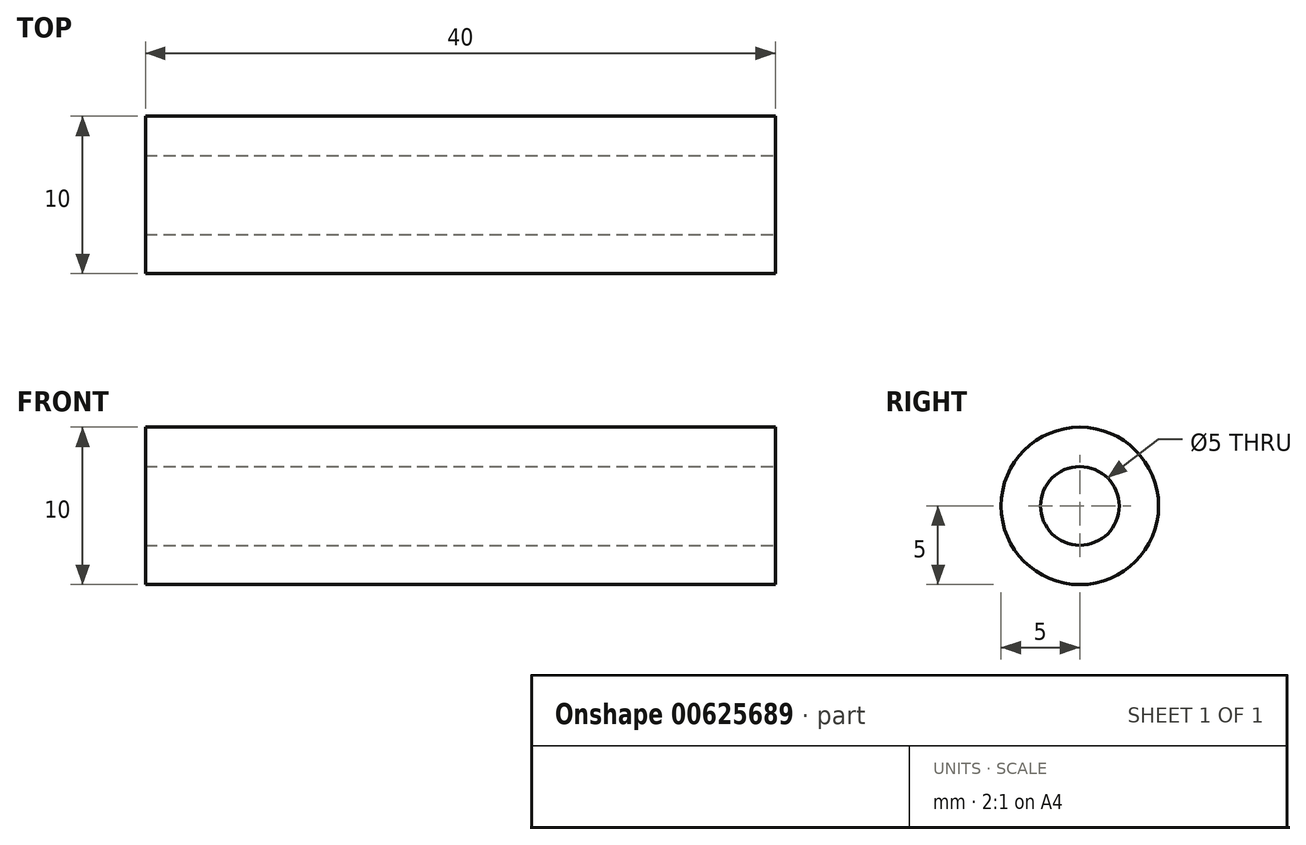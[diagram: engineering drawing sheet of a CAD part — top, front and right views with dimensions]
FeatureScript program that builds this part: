
annotation { "Feature Type Name" : "Feature", "Feature Type Description" : "" }
export const myFeature = defineFeature(function(context is Context, id is Id, definition is map)
    precondition{}
    {
        {
            var Q0;
            Q0=qCreatedBy(makeId("Right.planeOp"),FACE);
            var sketch = newSketch(context, id + "F0", { "sketchPlane" : qUnion([Q0])});
            skCircle(sketch, "E0", {"center": v(0, 0) * mm, "radius": 5 * mm});
            skSolve(sketch);
        }
        {
            var Q0;
            Q0 = qSketchRegion(id + "F0", true);
            extrude(context, id + "F1", {"entities" : qUnion([Q0]), "oppositeDirection" : true, "depth" : 40 * mm, "offsetDistance" : 25 * mm});
        }
        {
            var Q0;
            Q0=makeQuery(id+"F1.opExtrude","CAP_FACE",FACE,{"disambiguationData":[OSD([sQuery(id+"F0.wireOp",EDGE,"E0")])],"isStart":true});
            var sketch = newSketch(context, id + "F2", { "sketchPlane" : qUnion([Q0])});
            skCircle(sketch, "E1", {"center": v(0, 0) * mm, "radius": 2.5 * mm});
            skSolve(sketch);
        }
        {
            var Q0;
            Q0=sQuery(id+"F2.wireOp",VERTEX,"E1.center");
            var Q1;
            Q1=makeQuery(id+"F1.opExtrude","SWEPT_BODY",BODY,{"disambiguationData":[OSD([sQuery(id+"F0.wireOp",EDGE,"E0")])]});
            hole(context, id + "F3", {"style" : HoleStyle.SIMPLE, "endStyle" : HoleEndStyle.THROUGH, "holeDiameter" : 5 * mm, "majorDiameter" : 5 * mm, "isTappedThrough" : true, "tappedDepth" : 12 * mm, "tapClearance" : 3, "locations" : qUnion([Q0]), "scope" : qUnion([Q1])});
        }
    });
